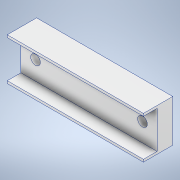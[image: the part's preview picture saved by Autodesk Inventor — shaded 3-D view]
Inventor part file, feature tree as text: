
AUTODESK INVENTOR PART (.ipt)
format: ipt  version: 2022.1 (Build 261234000, 234)  size: 124,928 bytes
history: native  units: mm
features: sketch x3, extrude x2, hole x1
ambient origin geometry x8: Origin, YZ Plane, XZ Plane, XY Plane, X Axis, Y Axis, Z Axis, Center Point
bodies: Solid1 (feature_tree)
feature tree (6):
  extrude  "Extrusion1"  Depth=14.85mm
  extrude  "Extrusion2"  TaperAngle=0.0deg  [1 undecoded]
  hole  "Hole1"  [1 undecoded]
  sketch  "Sketch1"  dims[d0=47.85mm d1=14.85mm]
  sketch  "Sketch3"  dims[d2=10.3mm d3=0.0mm]
  sketch  "Sketch4"  dims[d5=13.1mm d6=4.8mm d7=0.0mm d8=18.8mm d9=18.8mm d10=3.4mm d11=6.0mm d12=6.3mm d13=2.362mm d14=90.0deg d15=8.0mm d16=20.594885mm]
note: 2 required parameter values undecoded (feature->parameter linkage not recoverable at this tier; creation-order binding heuristic only, values carry confidence <= 0.55)
